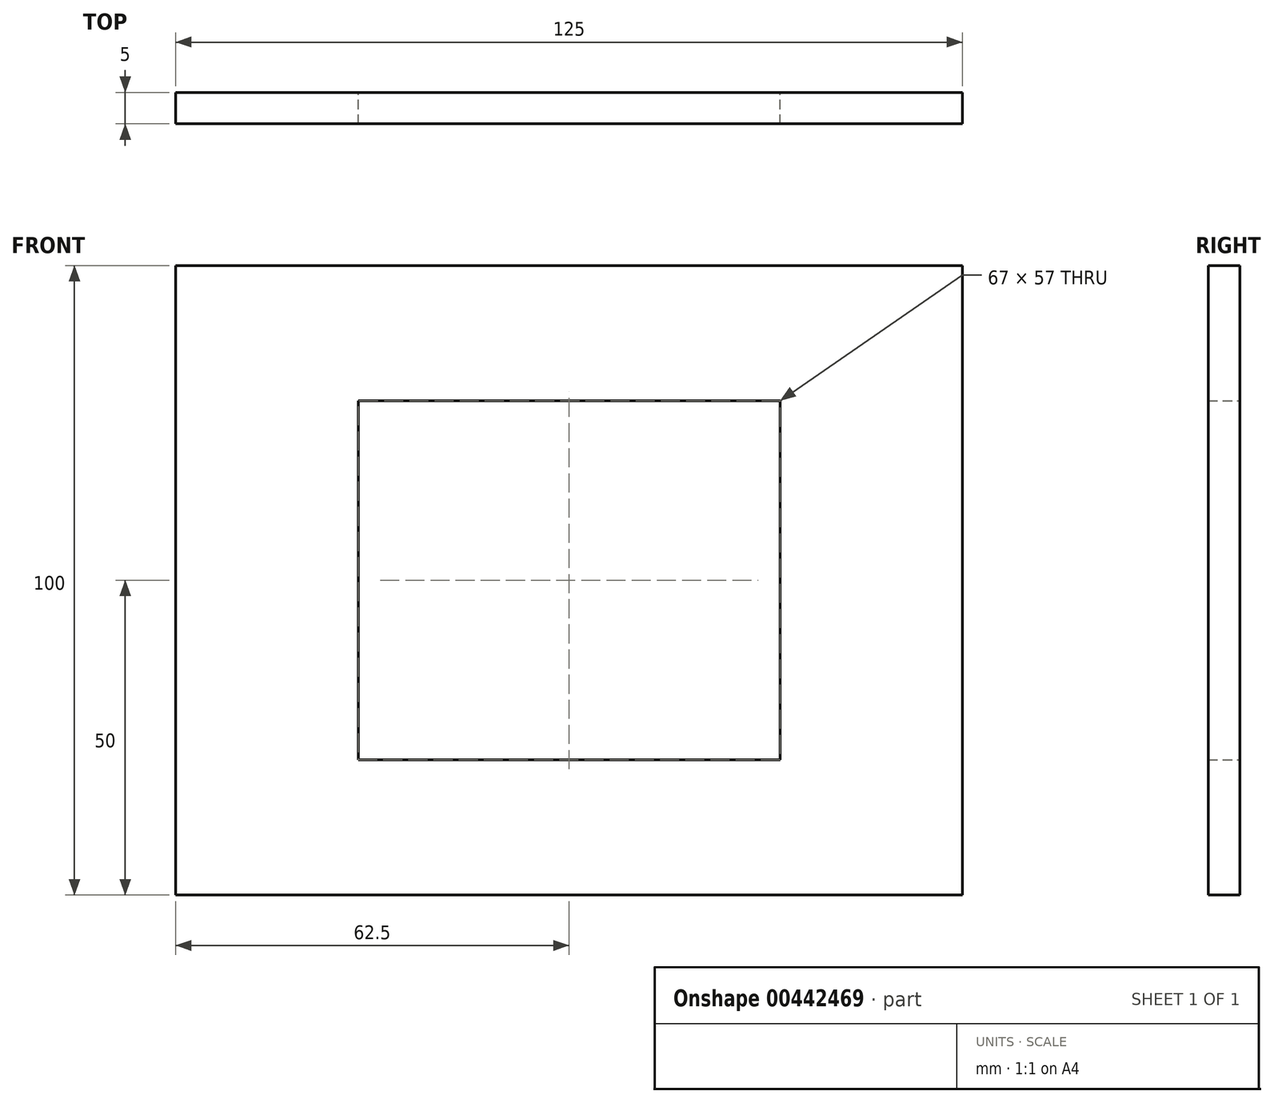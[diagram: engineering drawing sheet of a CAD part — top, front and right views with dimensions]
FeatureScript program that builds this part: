
annotation { "Feature Type Name" : "Feature", "Feature Type Description" : "" }
export const myFeature = defineFeature(function(context is Context, id is Id, definition is map)
    precondition{}
    {
        {
            var Q0;
            Q0=qCreatedBy(makeId("Front.planeOp"),FACE);
            var sketch = newSketch(context, id + "F0", { "sketchPlane" : qUnion([Q0])});
            skLineSegment(sketch, "E0.bottom", {"start": v(51.9, 39.25) * mm, "end": v(-51.9, 39.25) * mm, "construction": true});
            skLineSegment(sketch, "E0.top", {"start": v(51.9, -39.25) * mm, "end": v(-51.9, -39.25) * mm, "construction": true});
            skLineSegment(sketch, "E0.left", {"start": v(51.9, 39.25) * mm, "end": v(51.9, -39.25) * mm, "construction": true});
            skLineSegment(sketch, "E0.right", {"start": v(-51.9, 39.25) * mm, "end": v(-51.9, -39.25) * mm, "construction": true});
            skPoint(sketch, "E0.middle", {"position": v(0, 0) * mm});
            skLineSegment(sketch, "E1.bottom", {"start": v(33.5, 28.5) * mm, "end": v(-33.5, 28.5) * mm});
            skLineSegment(sketch, "E1.top", {"start": v(33.5, -28.5) * mm, "end": v(-33.5, -28.5) * mm});
            skLineSegment(sketch, "E1.left", {"start": v(33.5, 28.5) * mm, "end": v(33.5, -28.5) * mm});
            skLineSegment(sketch, "E1.right", {"start": v(-33.5, 28.5) * mm, "end": v(-33.5, -28.5) * mm});
            skLineSegment(sketch, "E2.bottom", {"start": v(62.5, 50) * mm, "end": v(-62.5, 50) * mm});
            skLineSegment(sketch, "E2.top", {"start": v(62.5, -50) * mm, "end": v(-62.5, -50) * mm});
            skLineSegment(sketch, "E2.left", {"start": v(62.5, 50) * mm, "end": v(62.5, -50) * mm});
            skLineSegment(sketch, "E2.right", {"start": v(-62.5, 50) * mm, "end": v(-62.5, -50) * mm});
            skSolve(sketch);
        }
        {
            var Q0;
            Q0 = qSketchRegion(id + "F0", true);
            extrude(context, id + "F1", {"entities" : qUnion([Q0]), "depth" : 5 * mm});
        }
    });
